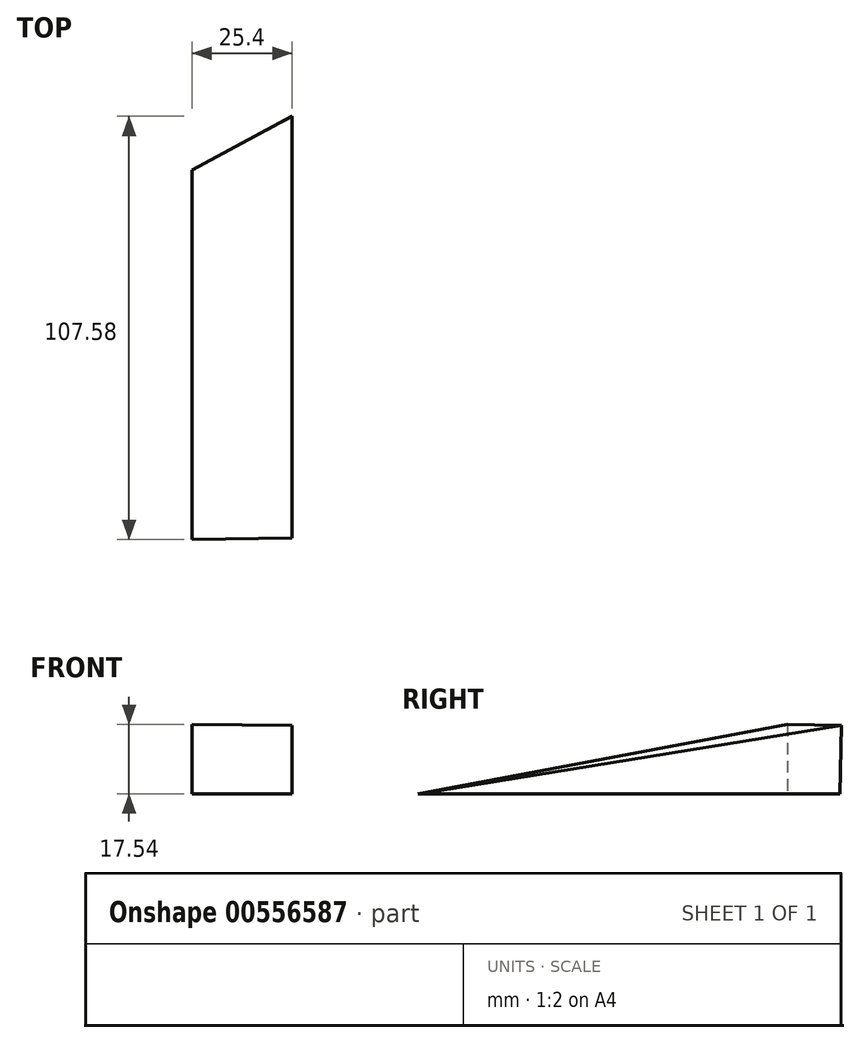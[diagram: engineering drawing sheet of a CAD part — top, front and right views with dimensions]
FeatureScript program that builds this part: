
annotation { "Feature Type Name" : "Feature", "Feature Type Description" : "" }
export const myFeature = defineFeature(function(context is Context, id is Id, definition is map)
    precondition{}
    {
        {
            var Q0;
            Q0=qCreatedBy(makeId("Right.planeOp"),FACE);
            var sketch = newSketch(context, id + "F0", { "sketchPlane" : qUnion([Q0])});
            skLineSegment(sketch, "E0", {"start": v(19.03, 17.54) * mm, "end": v(19.03, 0) * mm});
            skLineSegment(sketch, "E1", {"start": v(19.03, 0) * mm, "end": v(-74.89, 0) * mm});
            skLineSegment(sketch, "E2", {"start": v(-74.89, 0) * mm, "end": v(19.03, 17.54) * mm});
            skSolve(sketch);
        }
        {
            var Q0;
            Q0=qCreatedBy(makeId("Right.planeOp"),FACE);
            cPlane(context, id + "F1", {"entities" : qUnion([Q0]), "cplaneType" : CPlaneType.OFFSET, "offset" : 25.4 * mm, "width" : 152.4 * mm, "height" : 152.4 * mm});
        }
        {
            var Q0;
            Q0=qCreatedBy(id+"F1.planeOp",FACE);
            var sketch = newSketch(context, id + "F2", { "sketchPlane" : qUnion([Q0])});
            skLineSegment(sketch, "E3", {"start": v(32.69, 17.35) * mm, "end": v(32.69, 16.24) * mm});
            skLineSegment(sketch, "E4", {"start": v(32.69, 17.35) * mm, "end": v(-74.46, 0) * mm});
            skLineSegment(sketch, "E5", {"start": v(-74.46, 0) * mm, "end": v(32.28, 0) * mm});
            skLineSegment(sketch, "E6", {"start": v(32.69, 17.35) * mm, "end": v(32.28, 0) * mm});
            skSolve(sketch);
        }
        {
            var Q0;
            Q0=makeQuery(id+"F2.imprint","IMPRINT",FACE,{"disambiguationData":[TD([[makeQuery(id+"F2.imprint","IMPRINT",EDGE,{"derivedFrom":sQuery(id+"F2.wireOp",EDGE,"E4")}),1.0]])]});
            var Q1;
            Q1=makeQuery(id+"F0.imprint","IMPRINT",FACE,{"disambiguationData":[TD([[makeQuery(id+"F0.imprint","IMPRINT",EDGE,{"derivedFrom":sQuery(id+"F0.wireOp",EDGE,"E0")}),-1.0]])]});
            loft(context, id + "F3", {"sheetProfilesArray" : [{ "sheetProfileEntities" : qUnion([Q0]) }, { "sheetProfileEntities" : qUnion([Q1]) }]});
        }
        {
            var Q0;
            Q0=qCreatedBy(makeId("Right.planeOp"),FACE);
            cPlane(context, id + "F4", {"entities" : qUnion([Q0]), "cplaneType" : CPlaneType.OFFSET, "offset" : 25.5 * mm, "width" : 150 * mm, "height" : 150 * mm});
        }
    });
